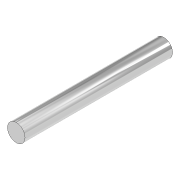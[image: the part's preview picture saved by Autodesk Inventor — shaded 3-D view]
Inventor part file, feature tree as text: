
AUTODESK INVENTOR PART (.ipt)
format: ipt  version: 2020 (Build 240168000, 168)  size: 78,336 bytes
history: native  units: in
note: dims shown in document units (in); Inventor stores cm internally (conversion verified against a paired STEP export)
features: extrude x1, sketch x1
ambient origin geometry x8: Origin, YZ Plane, XZ Plane, XY Plane, X Axis, Y Axis, Z Axis, Center Point
bodies: Solid1 (feature_tree)
feature tree (2):
  extrude  "Extrusion1"  Depth=1.6535in TaperAngle=0.0deg
  sketch  "Sketch1"  dims[d0=0.1969in d1=1.6535in d2=0.0in]
